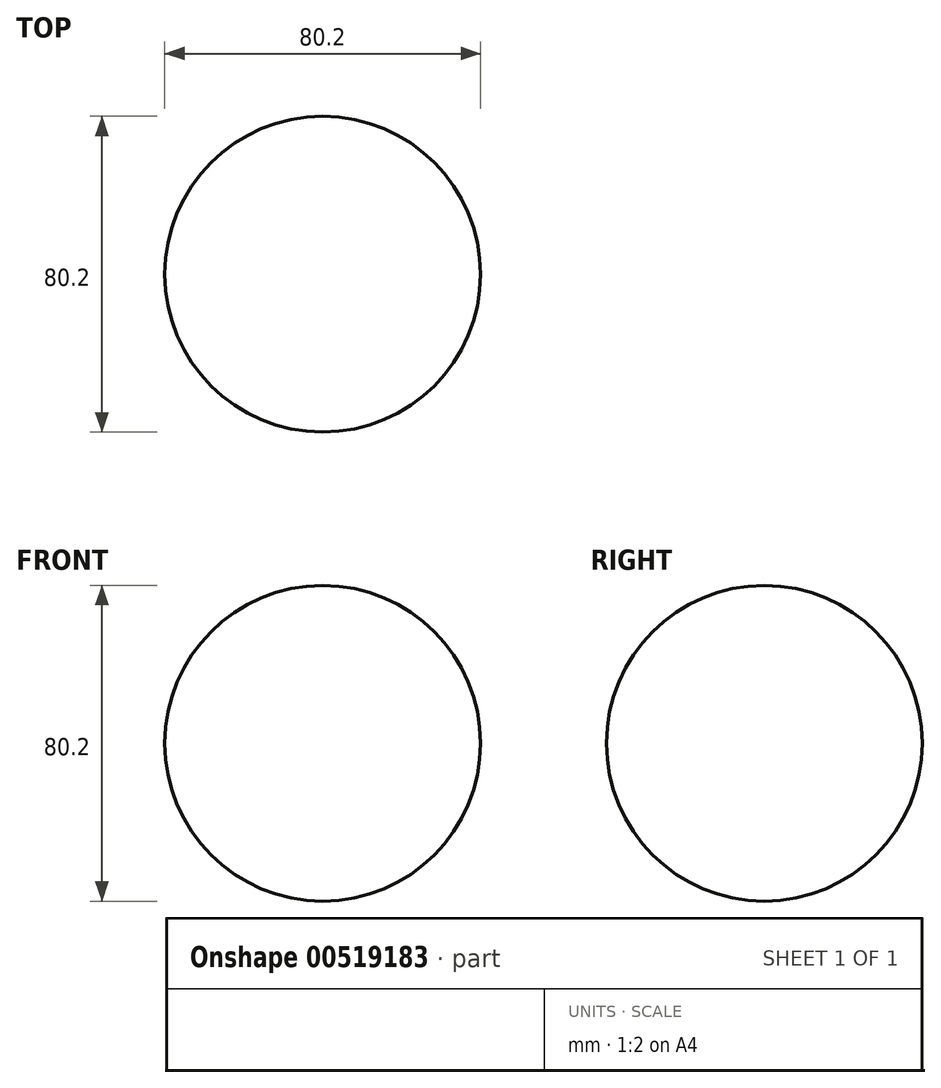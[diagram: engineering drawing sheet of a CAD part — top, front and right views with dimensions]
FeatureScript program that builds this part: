
annotation { "Feature Type Name" : "Feature", "Feature Type Description" : "" }
export const myFeature = defineFeature(function(context is Context, id is Id, definition is map)
    precondition{}
    {
        {
            var Q0;
            Q0=qCreatedBy(makeId("Top.planeOp"),FACE);
            var sketch = newSketch(context, id + "F0", { "sketchPlane" : qUnion([Q0])});
            skArc(sketch, "E0", {"start": v(0, -40.1) * mm, "mid": v(40.1, 0) * mm, "end": v(0, 40.1) * mm});
            skLineSegment(sketch, "E1", {"start": v(0, 40.1) * mm, "end": v(0, -40.1) * mm});
            skSolve(sketch);
        }
        {
            var Q0;
            Q0=makeQuery(id+"F0.imprint","IMPRINT",FACE,{"disambiguationData":[TD([[makeQuery(id+"F0.imprint","IMPRINT",EDGE,{"derivedFrom":sQuery(id+"F0.wireOp",EDGE,"E0")}),1.0]])]});
            var Q1;
            Q1=sQuery(id+"F0.wireOp",EDGE,"E1");
            revolve(context, id + "F1", {"entities" : qUnion([Q0]), "axis" : qUnion([Q1]), "revolveType" : RevolveType.FULL});
        }
    });
